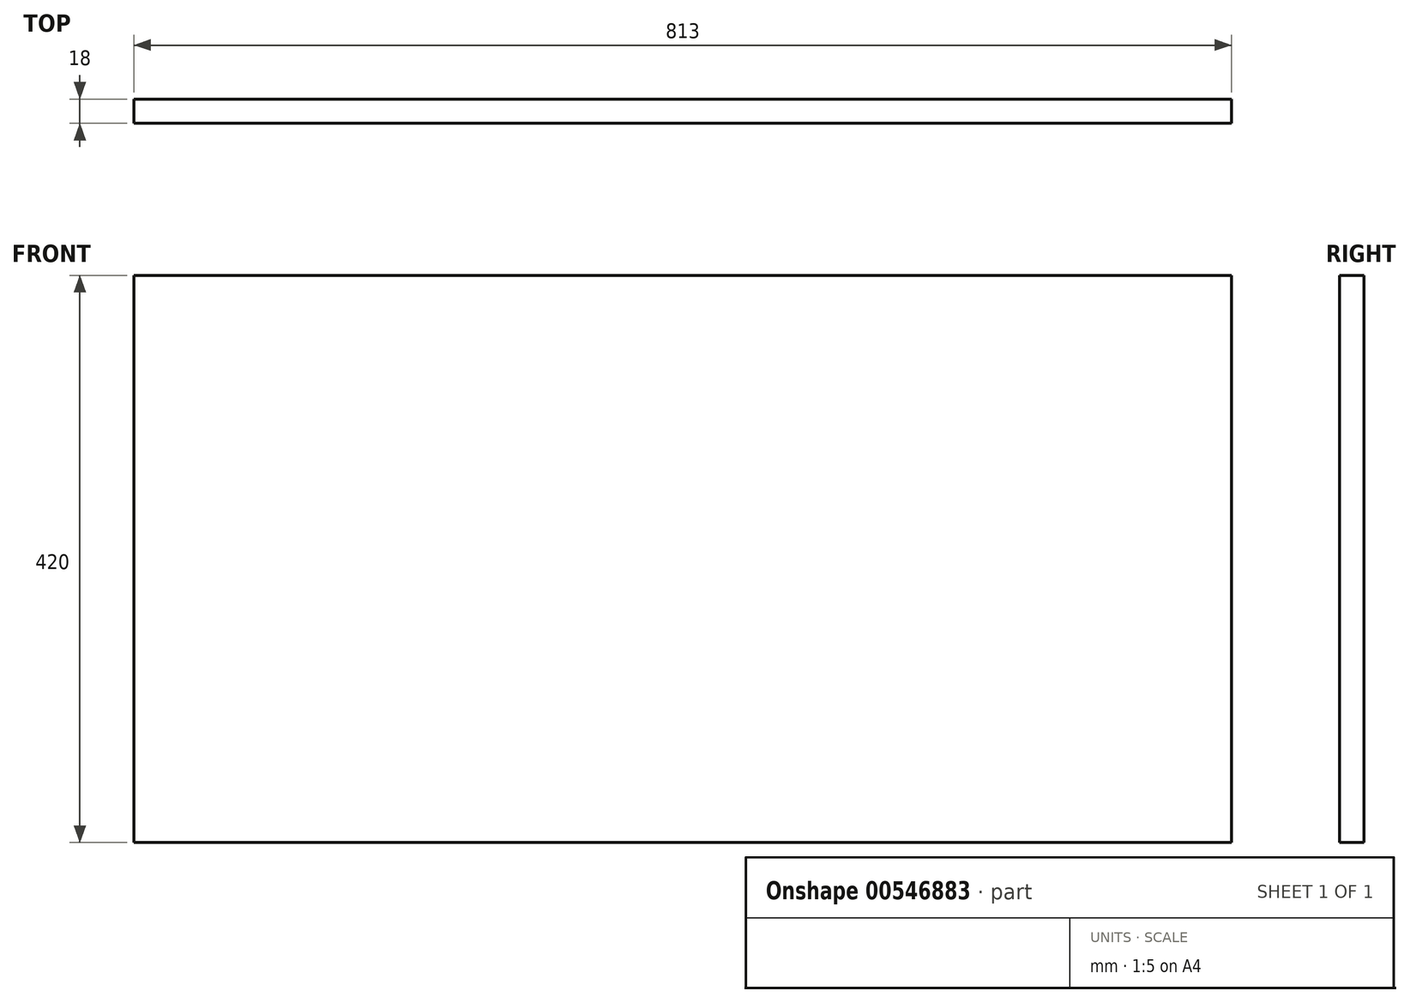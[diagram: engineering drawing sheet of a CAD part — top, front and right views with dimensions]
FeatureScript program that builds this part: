
annotation { "Feature Type Name" : "Feature", "Feature Type Description" : "" }
export const myFeature = defineFeature(function(context is Context, id is Id, definition is map)
    precondition{}
    {
        {
            var Q0;
            Q0=qCreatedBy(makeId("Front.planeOp"),FACE);
            var sketch = newSketch(context, id + "F0", { "sketchPlane" : qUnion([Q0])});
            skLineSegment(sketch, "E0.bottom", {"start": v(-402.35, -202.2) * mm, "end": v(410.65, -202.2) * mm});
            skLineSegment(sketch, "E0.top", {"start": v(-402.35, 217.8) * mm, "end": v(410.65, 217.8) * mm});
            skLineSegment(sketch, "E0.left", {"start": v(-402.35, -202.2) * mm, "end": v(-402.35, 217.8) * mm});
            skLineSegment(sketch, "E0.right", {"start": v(410.65, -202.2) * mm, "end": v(410.65, 217.8) * mm});
            skSolve(sketch);
        }
        {
            var Q0;
            Q0 = qSketchRegion(id + "F0", true);
            extrude(context, id + "F1", {"entities" : qUnion([Q0]), "depth" : 18 * mm, "offsetDistance" : 25 * mm});
        }
    });
